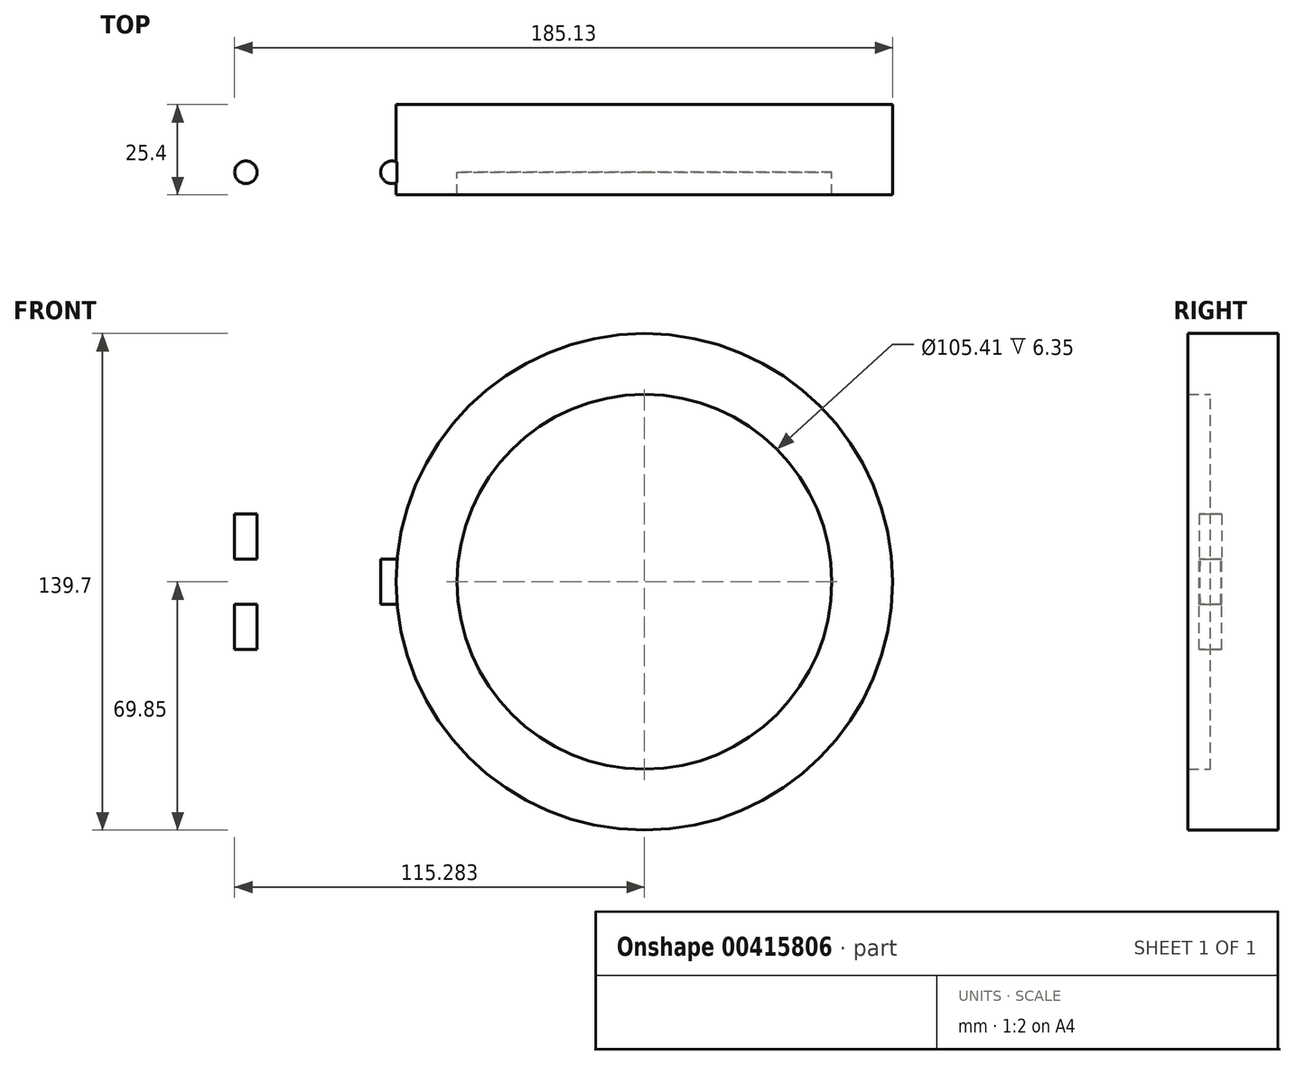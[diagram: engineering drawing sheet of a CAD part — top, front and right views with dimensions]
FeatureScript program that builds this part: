
annotation { "Feature Type Name" : "Feature", "Feature Type Description" : "" }
export const myFeature = defineFeature(function(context is Context, id is Id, definition is map)
    precondition{}
    {
        {
            var Q0;
            Q0=qCreatedBy(makeId("Top.planeOp"),FACE);
            var sketch = newSketch(context, id + "F0", { "sketchPlane" : qUnion([Q0])});
            skCircle(sketch, "E0", {"center": v(-76.2, 0) * mm, "radius": 3.18 * mm});
            skSolve(sketch);
        }
        {
            var Q0;
            Q0 = qSketchRegion(id + "F0", true);
            extrude(context, id + "F1", {"entities" : qUnion([Q0]), "depth" : 19.05 * mm, "hasSecondDirection" : true, "secondDirectionOppositeDirection" : false, "secondDirectionDepth" : 6.35 * mm});
        }
        {
            var Q0;
            Q0=qCreatedBy(makeId("Top.planeOp"),FACE);
            var sketch = newSketch(context, id + "F2", { "sketchPlane" : qUnion([Q0])});
            skCircle(sketch, "E1", {"center": v(-76.2, 0) * mm, "radius": 3.17 * mm});
            skSolve(sketch);
        }
        {
            var Q0;
            Q0 = qSketchRegion(id + "F2", true);
            extrude(context, id + "F3", {"entities" : qUnion([Q0]), "oppositeDirection" : true, "depth" : 19.05 * mm, "hasSecondDirection" : true, "secondDirectionOppositeDirection" : true, "secondDirectionDepth" : 6.35 * mm});
        }
        {
            var Q0;
            Q0=qCreatedBy(makeId("Top.planeOp"),FACE);
            var sketch = newSketch(context, id + "F4", { "sketchPlane" : qUnion([Q0])});
            skCircle(sketch, "E2", {"center": v(-35.13, 0) * mm, "radius": 3.18 * mm});
            skSolve(sketch);
        }
        {
            var Q0;
            Q0 = qSketchRegion(id + "F4", true);
            extrude(context, id + "F5", {"entities" : qUnion([Q0]), "oppositeDirection" : true, "depth" : 6.35 * mm, "hasSecondDirection" : true, "secondDirectionOppositeDirection" : false, "secondDirectionDepth" : 6.35 * mm});
        }
        {
            var Q0;
            Q0=qCreatedBy(makeId("Front.planeOp"),FACE);
            var sketch = newSketch(context, id + "F6", { "sketchPlane" : qUnion([Q0])});
            skCircle(sketch, "E3", {"center": v(35.9, 0) * mm, "radius": 69.85 * mm});
            skSolve(sketch);
        }
        {
            var Q0;
            Q0 = qSketchRegion(id + "F6", true);
            extrude(context, id + "F7", {"entities" : qUnion([Q0]), "operationType" : NewBodyOperationType.ADD, "oppositeDirection" : true, "depth" : 19.05 * mm});
        }
        {
            var Q0;
            Q0=makeQuery(id+"F7.opExtrude","CAP_FACE",FACE,{"disambiguationData":[OSD([sQuery(id+"F6.wireOp",EDGE,"E3")])],"isStart":true});
            var sketch = newSketch(context, id + "F8", { "sketchPlane" : qUnion([Q0])});
            skCircle(sketch, "E4", {"center": v(35.9, 0) * mm, "radius": 52.7 * mm});
            skCircle(sketch, "E5", {"center": v(35.9, 0) * mm, "radius": 69.85 * mm});
            skSolve(sketch);
        }
        {
            var Q0;
            Q0 = qSketchRegion(id + "F8", true);
            extrude(context, id + "F9", {"entities" : qUnion([Q0]), "operationType" : NewBodyOperationType.ADD, "depth" : 6.35 * mm});
        }
    });
